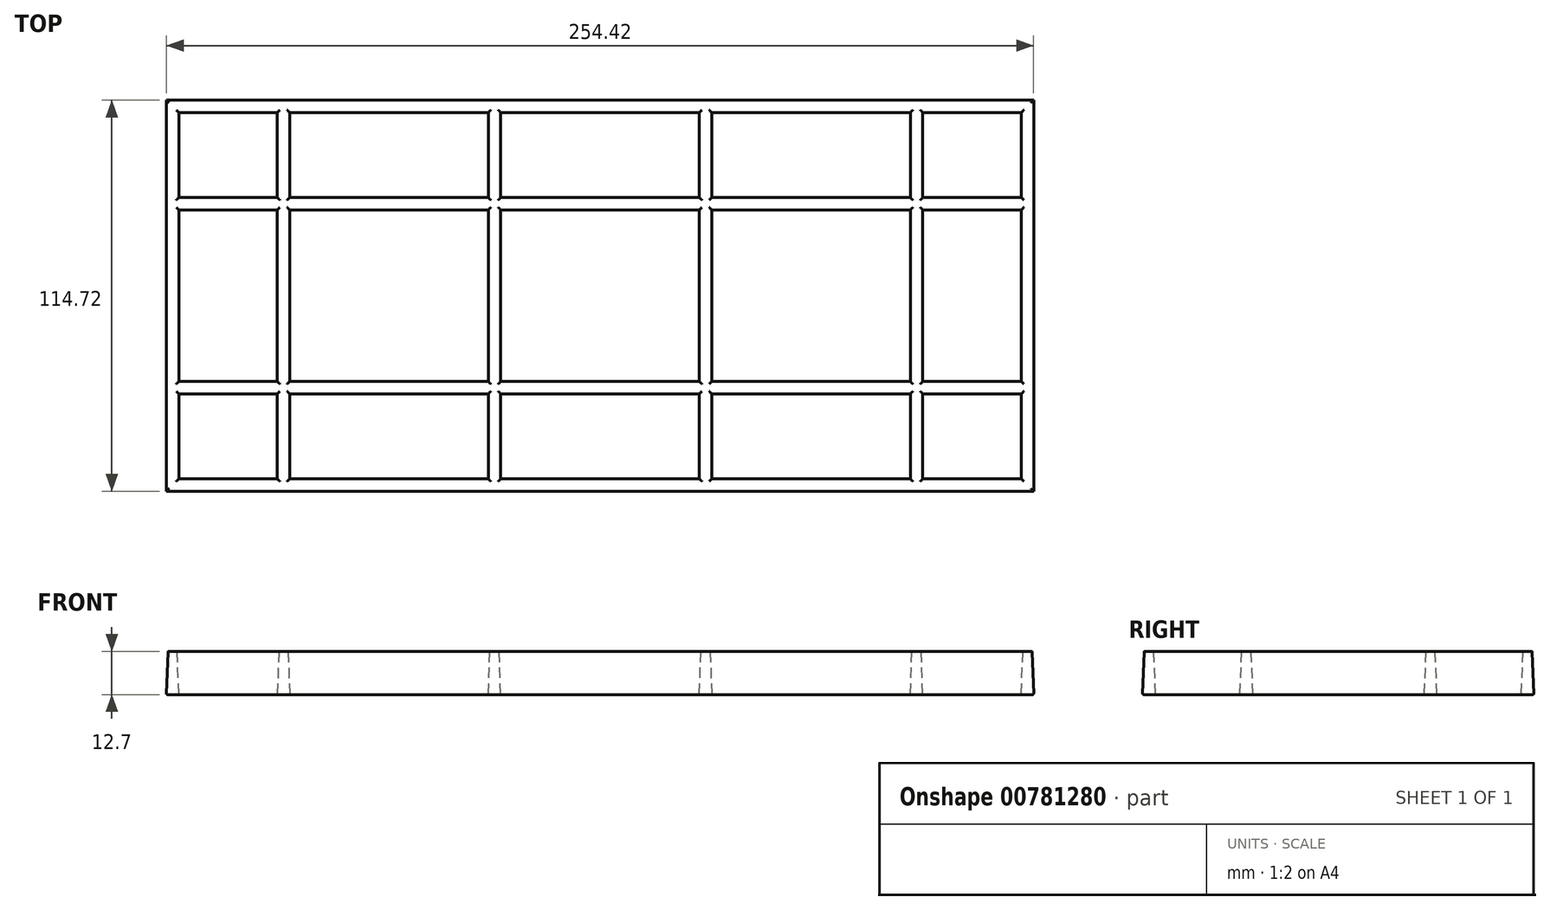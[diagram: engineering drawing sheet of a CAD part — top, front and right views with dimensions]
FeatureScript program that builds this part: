
annotation { "Feature Type Name" : "Feature", "Feature Type Description" : "" }
export const myFeature = defineFeature(function(context is Context, id is Id, definition is map)
    precondition{}
    {
        {
            var Q0;
            Q0=qCreatedBy(makeId("Top.planeOp"),FACE);
            var sketch = newSketch(context, id + "F0", { "sketchPlane" : qUnion([Q0])});
            skLineSegment(sketch, "E0.bottom", {"start": v(127, 57.15) * mm, "end": v(-127, 57.15) * mm});
            skLineSegment(sketch, "E0.top", {"start": v(127, -57.15) * mm, "end": v(-127, -57.15) * mm});
            skLineSegment(sketch, "E0.left", {"start": v(127, 57.15) * mm, "end": v(127, -57.15) * mm});
            skLineSegment(sketch, "E0.right", {"start": v(-127, 57.15) * mm, "end": v(-127, -57.15) * mm});
            skPoint(sketch, "E0.middle", {"position": v(0, 0) * mm});
            skLineSegment(sketch, "E1.0", {"start": v(123.82, 53.97) * mm, "end": v(-123.83, 53.98) * mm});
            skLineSegment(sketch, "E1.1", {"start": v(123.82, 53.97) * mm, "end": v(123.82, -53.97) * mm});
            skLineSegment(sketch, "E1.2", {"start": v(123.82, -53.98) * mm, "end": v(-123.83, -53.98) * mm});
            skLineSegment(sketch, "E1.3", {"start": v(-123.82, 53.98) * mm, "end": v(-123.83, -53.98) * mm});
            skLineSegment(sketch, "E2", {"start": v(-123.82, 26.99) * mm, "end": v(123.82, 26.99) * mm, "construction": true});
            skLineSegment(sketch, "E3", {"start": v(-123.83, 0) * mm, "end": v(123.82, 0) * mm, "construction": true});
            skLineSegment(sketch, "E4", {"start": v(-123.83, -26.99) * mm, "end": v(123.82, -26.99) * mm, "construction": true});
            skLineSegment(sketch, "E5", {"start": v(-92.87, 53.98) * mm, "end": v(-92.87, -53.98) * mm, "construction": true});
            skLineSegment(sketch, "E6", {"start": v(-61.91, 53.98) * mm, "end": v(-61.91, -53.98) * mm, "construction": true});
            skLineSegment(sketch, "E7", {"start": v(-30.96, 53.98) * mm, "end": v(-30.96, -53.98) * mm, "construction": true});
            skLineSegment(sketch, "E8", {"start": v(0, 53.98) * mm, "end": v(0, -53.98) * mm, "construction": true});
            skLineSegment(sketch, "E9", {"start": v(30.96, 53.98) * mm, "end": v(30.96, -53.98) * mm, "construction": true});
            skLineSegment(sketch, "E10", {"start": v(61.91, -53.98) * mm, "end": v(61.91, 53.98) * mm, "construction": true});
            skLineSegment(sketch, "E11", {"start": v(92.87, 53.97) * mm, "end": v(92.87, -53.97) * mm, "construction": true});
            skLineSegment(sketch, "E12.bottom", {"start": v(123.82, 28.58) * mm, "end": v(-123.82, 28.58) * mm});
            skLineSegment(sketch, "E12.top", {"start": v(123.82, 25.4) * mm, "end": v(-123.82, 25.4) * mm});
            skLineSegment(sketch, "E12.left", {"start": v(123.82, 28.58) * mm, "end": v(123.82, 25.4) * mm});
            skLineSegment(sketch, "E12.right", {"start": v(-123.82, 28.58) * mm, "end": v(-123.82, 25.4) * mm});
            skPoint(sketch, "E12.middle", {"position": v(0, 26.99) * mm});
            skLineSegment(sketch, "E13.bottom", {"start": v(123.82, 1.59) * mm, "end": v(-123.82, 1.59) * mm});
            skLineSegment(sketch, "E13.top", {"start": v(123.82, -1.59) * mm, "end": v(-123.82, -1.59) * mm});
            skLineSegment(sketch, "E13.left", {"start": v(123.82, 1.59) * mm, "end": v(123.82, -1.59) * mm});
            skLineSegment(sketch, "E13.right", {"start": v(-123.82, 1.59) * mm, "end": v(-123.82, -1.59) * mm});
            skLineSegment(sketch, "E14.bottom", {"start": v(123.82, -25.4) * mm, "end": v(-123.82, -25.4) * mm});
            skLineSegment(sketch, "E14.top", {"start": v(123.82, -28.57) * mm, "end": v(-123.82, -28.57) * mm});
            skLineSegment(sketch, "E14.left", {"start": v(123.82, -25.4) * mm, "end": v(123.82, -28.57) * mm});
            skLineSegment(sketch, "E14.right", {"start": v(-123.83, -25.4) * mm, "end": v(-123.83, -28.57) * mm});
            skPoint(sketch, "E14.middle", {"position": v(0, -26.99) * mm});
            skLineSegment(sketch, "E15.bottom", {"start": v(-91.28, 53.98) * mm, "end": v(-94.46, 53.98) * mm});
            skLineSegment(sketch, "E15.top", {"start": v(-91.28, -53.98) * mm, "end": v(-94.46, -53.98) * mm});
            skLineSegment(sketch, "E15.left", {"start": v(-91.28, 53.98) * mm, "end": v(-91.28, -53.98) * mm});
            skLineSegment(sketch, "E15.right", {"start": v(-94.46, 53.98) * mm, "end": v(-94.46, -53.98) * mm});
            skPoint(sketch, "E15.middle", {"position": v(-92.87, 0) * mm});
            skLineSegment(sketch, "E16.bottom", {"start": v(-60.32, 53.98) * mm, "end": v(-63.5, 53.98) * mm});
            skLineSegment(sketch, "E16.top", {"start": v(-60.32, -53.98) * mm, "end": v(-63.5, -53.98) * mm});
            skLineSegment(sketch, "E16.left", {"start": v(-60.32, 53.98) * mm, "end": v(-60.32, -53.98) * mm});
            skLineSegment(sketch, "E16.right", {"start": v(-63.5, 53.98) * mm, "end": v(-63.5, -53.98) * mm});
            skPoint(sketch, "E16.middle", {"position": v(-61.91, 0) * mm});
            skLineSegment(sketch, "E17.bottom", {"start": v(-29.37, 53.98) * mm, "end": v(-32.54, 53.98) * mm});
            skLineSegment(sketch, "E17.top", {"start": v(-29.37, -53.98) * mm, "end": v(-32.54, -53.98) * mm});
            skLineSegment(sketch, "E17.left", {"start": v(-29.37, 53.98) * mm, "end": v(-29.37, -53.98) * mm});
            skLineSegment(sketch, "E17.right", {"start": v(-32.54, 53.98) * mm, "end": v(-32.54, -53.98) * mm});
            skPoint(sketch, "E17.middle", {"position": v(-30.96, 0) * mm});
            skLineSegment(sketch, "E18.bottom", {"start": v(1.59, 53.98) * mm, "end": v(-1.59, 53.98) * mm});
            skLineSegment(sketch, "E18.top", {"start": v(1.59, -53.98) * mm, "end": v(-1.59, -53.98) * mm});
            skLineSegment(sketch, "E18.left", {"start": v(1.59, 53.98) * mm, "end": v(1.59, -53.98) * mm});
            skLineSegment(sketch, "E18.right", {"start": v(-1.59, 53.98) * mm, "end": v(-1.59, -53.98) * mm});
            skLineSegment(sketch, "E19.bottom", {"start": v(32.54, 53.98) * mm, "end": v(29.37, 53.98) * mm});
            skLineSegment(sketch, "E19.top", {"start": v(32.54, -53.98) * mm, "end": v(29.37, -53.98) * mm});
            skLineSegment(sketch, "E19.left", {"start": v(32.54, 53.98) * mm, "end": v(32.54, -53.98) * mm});
            skLineSegment(sketch, "E19.right", {"start": v(29.37, 53.98) * mm, "end": v(29.37, -53.98) * mm});
            skPoint(sketch, "E19.middle", {"position": v(30.96, 0) * mm});
            skLineSegment(sketch, "E20.bottom", {"start": v(63.5, 53.98) * mm, "end": v(60.33, 53.98) * mm});
            skLineSegment(sketch, "E20.top", {"start": v(63.5, -53.98) * mm, "end": v(60.33, -53.98) * mm});
            skLineSegment(sketch, "E20.left", {"start": v(63.5, 53.98) * mm, "end": v(63.5, -53.98) * mm});
            skLineSegment(sketch, "E20.right", {"start": v(60.33, 53.98) * mm, "end": v(60.33, -53.98) * mm});
            skPoint(sketch, "E20.middle", {"position": v(61.91, 0) * mm});
            skLineSegment(sketch, "E21.bottom", {"start": v(94.46, 53.97) * mm, "end": v(91.28, 53.97) * mm});
            skLineSegment(sketch, "E21.top", {"start": v(94.46, -53.97) * mm, "end": v(91.28, -53.97) * mm});
            skLineSegment(sketch, "E21.left", {"start": v(94.46, 53.98) * mm, "end": v(94.46, -53.98) * mm});
            skLineSegment(sketch, "E21.right", {"start": v(91.28, 53.98) * mm, "end": v(91.28, -53.98) * mm});
            skPoint(sketch, "E21.middle", {"position": v(92.87, 0) * mm});
            skSolve(sketch);
        }
        {
            var Q0;
            Q0=makeQuery(id+"F0.imprint","IMPRINT",FACE,{"disambiguationData":[TD([[makeQuery(id+"F0.imprint","IMPRINT",EDGE,{"derivedFrom":sQuery(id+"F0.wireOp",EDGE,"E0.bottom")}),1.0]])]});
            var Q1;
            {var subQ0=sQuery(id+"F0.wireOp",EDGE,"E20.left");var subQ1=sQuery(id+"F0.wireOp",EDGE,"E12.bottom");var subQ2=makeQuery(id+"F0.imprint","INTERSECT",VERTEX,{"derivedFrom":[subQ1,subQ0]});Q1=makeQuery(id+"F0.imprint","IMPRINT",FACE,{"disambiguationData":[TD([[makeQuery(id+"F0.imprint","IMPRINT",EDGE,{"disambiguationData":[TD([[subQ2,-1.0]])],"derivedFrom":subQ1}),1.0]])]});}
            var Q2;
            {var subQ0=sQuery(id+"F0.wireOp",EDGE,"E18.left");var subQ1=sQuery(id+"F0.wireOp",EDGE,"E12.bottom");var subQ2=makeQuery(id+"F0.imprint","INTERSECT",VERTEX,{"derivedFrom":[subQ1,subQ0]});Q2=makeQuery(id+"F0.imprint","IMPRINT",FACE,{"disambiguationData":[TD([[makeQuery(id+"F0.imprint","IMPRINT",EDGE,{"disambiguationData":[TD([[subQ2,-1.0]])],"derivedFrom":subQ1}),1.0]])]});}
            var Q3;
            {var subQ0=sQuery(id+"F0.wireOp",EDGE,"E16.right");var subQ1=sQuery(id+"F0.wireOp",EDGE,"E12.bottom");var subQ2=makeQuery(id+"F0.imprint","INTERSECT",VERTEX,{"derivedFrom":[subQ1,subQ0]});Q3=makeQuery(id+"F0.imprint","IMPRINT",FACE,{"disambiguationData":[TD([[makeQuery(id+"F0.imprint","IMPRINT",EDGE,{"disambiguationData":[TD([[subQ2,1.0]])],"derivedFrom":subQ1}),1.0]])]});}
            var Q4;
            {var subQ0=sQuery(id+"F0.wireOp",EDGE,"E21.left");var subQ1=sQuery(id+"F0.wireOp",EDGE,"E13.bottom");var subQ2=makeQuery(id+"F0.imprint","INTERSECT",VERTEX,{"derivedFrom":[subQ1,subQ0]});Q4=makeQuery(id+"F0.imprint","IMPRINT",FACE,{"disambiguationData":[TD([[makeQuery(id+"F0.imprint","IMPRINT",EDGE,{"disambiguationData":[TD([[subQ2,-1.0]])],"derivedFrom":subQ1}),1.0]])]});}
            var Q5;
            {var subQ0=sQuery(id+"F0.wireOp",EDGE,"E19.right");var subQ1=sQuery(id+"F0.wireOp",EDGE,"E13.bottom");var subQ2=makeQuery(id+"F0.imprint","INTERSECT",VERTEX,{"derivedFrom":[subQ1,subQ0]});Q5=makeQuery(id+"F0.imprint","IMPRINT",FACE,{"disambiguationData":[TD([[makeQuery(id+"F0.imprint","IMPRINT",EDGE,{"disambiguationData":[TD([[subQ2,1.0]])],"derivedFrom":subQ1}),1.0]])]});}
            var Q6;
            {var subQ0=sQuery(id+"F0.wireOp",EDGE,"E15.right");var subQ1=sQuery(id+"F0.wireOp",EDGE,"E13.bottom");var subQ2=makeQuery(id+"F0.imprint","INTERSECT",VERTEX,{"derivedFrom":[subQ1,subQ0]});Q6=makeQuery(id+"F0.imprint","IMPRINT",FACE,{"disambiguationData":[TD([[makeQuery(id+"F0.imprint","IMPRINT",EDGE,{"disambiguationData":[TD([[subQ2,1.0]])],"derivedFrom":subQ1}),1.0]])]});}
            var Q7;
            {var subQ0=sQuery(id+"F0.wireOp",EDGE,"E17.right");var subQ1=sQuery(id+"F0.wireOp",EDGE,"E13.bottom");var subQ2=makeQuery(id+"F0.imprint","INTERSECT",VERTEX,{"derivedFrom":[subQ1,subQ0]});Q7=makeQuery(id+"F0.imprint","IMPRINT",FACE,{"disambiguationData":[TD([[makeQuery(id+"F0.imprint","IMPRINT",EDGE,{"disambiguationData":[TD([[subQ2,1.0]])],"derivedFrom":subQ1}),1.0]])]});}
            var Q8;
            {var subQ0=sQuery(id+"F0.wireOp",EDGE,"E20.left");var subQ1=sQuery(id+"F0.wireOp",EDGE,"E14.bottom");var subQ2=makeQuery(id+"F0.imprint","INTERSECT",VERTEX,{"derivedFrom":[subQ1,subQ0]});Q8=makeQuery(id+"F0.imprint","IMPRINT",FACE,{"disambiguationData":[TD([[makeQuery(id+"F0.imprint","IMPRINT",EDGE,{"disambiguationData":[TD([[subQ2,-1.0]])],"derivedFrom":subQ1}),1.0]])]});}
            var Q9;
            {var subQ0=sQuery(id+"F0.wireOp",EDGE,"E18.left");var subQ1=sQuery(id+"F0.wireOp",EDGE,"E14.bottom");var subQ2=makeQuery(id+"F0.imprint","INTERSECT",VERTEX,{"derivedFrom":[subQ1,subQ0]});Q9=makeQuery(id+"F0.imprint","IMPRINT",FACE,{"disambiguationData":[TD([[makeQuery(id+"F0.imprint","IMPRINT",EDGE,{"disambiguationData":[TD([[subQ2,-1.0]])],"derivedFrom":subQ1}),1.0]])]});}
            var Q10;
            {var subQ0=sQuery(id+"F0.wireOp",EDGE,"E16.left");var subQ1=sQuery(id+"F0.wireOp",EDGE,"E14.bottom");var subQ2=makeQuery(id+"F0.imprint","INTERSECT",VERTEX,{"derivedFrom":[subQ1,subQ0]});Q10=makeQuery(id+"F0.imprint","IMPRINT",FACE,{"disambiguationData":[TD([[makeQuery(id+"F0.imprint","IMPRINT",EDGE,{"disambiguationData":[TD([[subQ2,-1.0]])],"derivedFrom":subQ1}),1.0]])]});}
            var Q11;
            {var subQ0=sQuery(id+"F0.wireOp",EDGE,"E15.right");var subQ1=sQuery(id+"F0.wireOp",EDGE,"E12.bottom");var subQ2=makeQuery(id+"F0.imprint","INTERSECT",VERTEX,{"derivedFrom":[subQ1,subQ0]});Q11=makeQuery(id+"F0.imprint","IMPRINT",FACE,{"disambiguationData":[TD([[makeQuery(id+"F0.imprint","IMPRINT",EDGE,{"disambiguationData":[TD([[subQ2,1.0]])],"derivedFrom":subQ1}),1.0]])]});}
            var Q12;
            {var subQ0=sQuery(id+"F0.wireOp",EDGE,"E12.top");var subQ1=sQuery(id+"F0.wireOp",EDGE,"E1.3");var subQ2=makeQuery(id+"F0.imprint","INTERSECT",VERTEX,{"derivedFrom":[subQ1,subQ0]});Q12=makeQuery(id+"F0.imprint","IMPRINT",FACE,{"disambiguationData":[TD([[makeQuery(id+"F0.imprint","IMPRINT",EDGE,{"disambiguationData":[TD([[subQ2,1.0]])],"derivedFrom":subQ1}),1.0]])]});}
            var Q13;
            {var subQ0=sQuery(id+"F0.wireOp",EDGE,"E15.right");var subQ1=sQuery(id+"F0.wireOp",EDGE,"E1.0");var subQ2=makeQuery(id+"F0.imprint","INTERSECT",VERTEX,{"derivedFrom":[subQ1,subQ0]});Q13=makeQuery(id+"F0.imprint","IMPRINT",FACE,{"disambiguationData":[TD([[makeQuery(id+"F0.imprint","IMPRINT",EDGE,{"disambiguationData":[TD([[subQ2,1.0]])],"derivedFrom":subQ1}),1.0]])]});}
            var Q14;
            {var subQ0=sQuery(id+"F0.wireOp",EDGE,"E15.right");var subQ1=sQuery(id+"F0.wireOp",EDGE,"E12.top");var subQ2=makeQuery(id+"F0.imprint","INTERSECT",VERTEX,{"derivedFrom":[subQ1,subQ0]});Q14=makeQuery(id+"F0.imprint","IMPRINT",FACE,{"disambiguationData":[TD([[makeQuery(id+"F0.imprint","IMPRINT",EDGE,{"disambiguationData":[TD([[subQ2,1.0]])],"derivedFrom":subQ1}),1.0]])]});}
            var Q15;
            {var subQ0=sQuery(id+"F0.wireOp",EDGE,"E16.right");var subQ1=sQuery(id+"F0.wireOp",EDGE,"E12.bottom");var subQ2=makeQuery(id+"F0.imprint","INTERSECT",VERTEX,{"derivedFrom":[subQ1,subQ0]});Q15=makeQuery(id+"F0.imprint","IMPRINT",FACE,{"disambiguationData":[TD([[makeQuery(id+"F0.imprint","IMPRINT",EDGE,{"disambiguationData":[TD([[subQ2,-1.0]])],"derivedFrom":subQ1}),1.0]])]});}
            var Q16;
            {var subQ0=sQuery(id+"F0.wireOp",EDGE,"E15.right");var subQ1=sQuery(id+"F0.wireOp",EDGE,"E13.top");var subQ2=makeQuery(id+"F0.imprint","INTERSECT",VERTEX,{"derivedFrom":[subQ1,subQ0]});Q16=makeQuery(id+"F0.imprint","IMPRINT",FACE,{"disambiguationData":[TD([[makeQuery(id+"F0.imprint","IMPRINT",EDGE,{"disambiguationData":[TD([[subQ2,1.0]])],"derivedFrom":subQ1}),1.0]])]});}
            var Q17;
            {var subQ0=sQuery(id+"F0.wireOp",EDGE,"E15.right");var subQ1=sQuery(id+"F0.wireOp",EDGE,"E14.bottom");var subQ2=makeQuery(id+"F0.imprint","INTERSECT",VERTEX,{"derivedFrom":[subQ1,subQ0]});Q17=makeQuery(id+"F0.imprint","IMPRINT",FACE,{"disambiguationData":[TD([[makeQuery(id+"F0.imprint","IMPRINT",EDGE,{"disambiguationData":[TD([[subQ2,1.0]])],"derivedFrom":subQ1}),1.0]])]});}
            var Q18;
            {var subQ0=sQuery(id+"F0.wireOp",EDGE,"E15.right");var subQ1=sQuery(id+"F0.wireOp",EDGE,"E1.2");var subQ2=makeQuery(id+"F0.imprint","INTERSECT",VERTEX,{"derivedFrom":[subQ1,subQ0]});Q18=makeQuery(id+"F0.imprint","IMPRINT",FACE,{"disambiguationData":[TD([[makeQuery(id+"F0.imprint","IMPRINT",EDGE,{"disambiguationData":[TD([[subQ2,1.0]])],"derivedFrom":subQ1}),-1.0]])]});}
            var Q19;
            {var subQ0=sQuery(id+"F0.wireOp",EDGE,"E14.top");var subQ1=sQuery(id+"F0.wireOp",EDGE,"E1.3");var subQ2=makeQuery(id+"F0.imprint","INTERSECT",VERTEX,{"derivedFrom":[subQ1,subQ0]});Q19=makeQuery(id+"F0.imprint","IMPRINT",FACE,{"disambiguationData":[TD([[makeQuery(id+"F0.imprint","IMPRINT",EDGE,{"disambiguationData":[TD([[subQ2,1.0]])],"derivedFrom":subQ1}),1.0]])]});}
            var Q20;
            {var subQ0=sQuery(id+"F0.wireOp",EDGE,"E16.right");var subQ1=sQuery(id+"F0.wireOp",EDGE,"E14.bottom");var subQ2=makeQuery(id+"F0.imprint","INTERSECT",VERTEX,{"derivedFrom":[subQ1,subQ0]});Q20=makeQuery(id+"F0.imprint","IMPRINT",FACE,{"disambiguationData":[TD([[makeQuery(id+"F0.imprint","IMPRINT",EDGE,{"disambiguationData":[TD([[subQ2,-1.0]])],"derivedFrom":subQ1}),1.0]])]});}
            var Q21;
            {var subQ0=sQuery(id+"F0.wireOp",EDGE,"E17.right");var subQ1=sQuery(id+"F0.wireOp",EDGE,"E12.bottom");var subQ2=makeQuery(id+"F0.imprint","INTERSECT",VERTEX,{"derivedFrom":[subQ1,subQ0]});Q21=makeQuery(id+"F0.imprint","IMPRINT",FACE,{"disambiguationData":[TD([[makeQuery(id+"F0.imprint","IMPRINT",EDGE,{"disambiguationData":[TD([[subQ2,-1.0]])],"derivedFrom":subQ1}),1.0]])]});}
            var Q22;
            {var subQ0=sQuery(id+"F0.wireOp",EDGE,"E17.right");var subQ1=sQuery(id+"F0.wireOp",EDGE,"E1.0");var subQ2=makeQuery(id+"F0.imprint","INTERSECT",VERTEX,{"derivedFrom":[subQ1,subQ0]});Q22=makeQuery(id+"F0.imprint","IMPRINT",FACE,{"disambiguationData":[TD([[makeQuery(id+"F0.imprint","IMPRINT",EDGE,{"disambiguationData":[TD([[subQ2,1.0]])],"derivedFrom":subQ1}),1.0]])]});}
            var Q23;
            {var subQ0=sQuery(id+"F0.wireOp",EDGE,"E17.right");var subQ1=sQuery(id+"F0.wireOp",EDGE,"E12.top");var subQ2=makeQuery(id+"F0.imprint","INTERSECT",VERTEX,{"derivedFrom":[subQ1,subQ0]});Q23=makeQuery(id+"F0.imprint","IMPRINT",FACE,{"disambiguationData":[TD([[makeQuery(id+"F0.imprint","IMPRINT",EDGE,{"disambiguationData":[TD([[subQ2,1.0]])],"derivedFrom":subQ1}),1.0]])]});}
            var Q24;
            {var subQ0=sQuery(id+"F0.wireOp",EDGE,"E17.left");var subQ1=sQuery(id+"F0.wireOp",EDGE,"E12.bottom");var subQ2=makeQuery(id+"F0.imprint","INTERSECT",VERTEX,{"derivedFrom":[subQ1,subQ0]});Q24=makeQuery(id+"F0.imprint","IMPRINT",FACE,{"disambiguationData":[TD([[makeQuery(id+"F0.imprint","IMPRINT",EDGE,{"disambiguationData":[TD([[subQ2,1.0]])],"derivedFrom":subQ1}),1.0]])]});}
            var Q25;
            {var subQ0=sQuery(id+"F0.wireOp",EDGE,"E17.right");var subQ1=sQuery(id+"F0.wireOp",EDGE,"E13.top");var subQ2=makeQuery(id+"F0.imprint","INTERSECT",VERTEX,{"derivedFrom":[subQ1,subQ0]});Q25=makeQuery(id+"F0.imprint","IMPRINT",FACE,{"disambiguationData":[TD([[makeQuery(id+"F0.imprint","IMPRINT",EDGE,{"disambiguationData":[TD([[subQ2,1.0]])],"derivedFrom":subQ1}),1.0]])]});}
            var Q26;
            {var subQ0=sQuery(id+"F0.wireOp",EDGE,"E17.right");var subQ1=sQuery(id+"F0.wireOp",EDGE,"E14.bottom");var subQ2=makeQuery(id+"F0.imprint","INTERSECT",VERTEX,{"derivedFrom":[subQ1,subQ0]});Q26=makeQuery(id+"F0.imprint","IMPRINT",FACE,{"disambiguationData":[TD([[makeQuery(id+"F0.imprint","IMPRINT",EDGE,{"disambiguationData":[TD([[subQ2,1.0]])],"derivedFrom":subQ1}),1.0]])]});}
            var Q27;
            {var subQ0=sQuery(id+"F0.wireOp",EDGE,"E17.right");var subQ1=sQuery(id+"F0.wireOp",EDGE,"E14.bottom");var subQ2=makeQuery(id+"F0.imprint","INTERSECT",VERTEX,{"derivedFrom":[subQ1,subQ0]});Q27=makeQuery(id+"F0.imprint","IMPRINT",FACE,{"disambiguationData":[TD([[makeQuery(id+"F0.imprint","IMPRINT",EDGE,{"disambiguationData":[TD([[subQ2,-1.0]])],"derivedFrom":subQ1}),1.0]])]});}
            var Q28;
            {var subQ0=sQuery(id+"F0.wireOp",EDGE,"E17.right");var subQ1=sQuery(id+"F0.wireOp",EDGE,"E1.2");var subQ2=makeQuery(id+"F0.imprint","INTERSECT",VERTEX,{"derivedFrom":[subQ1,subQ0]});Q28=makeQuery(id+"F0.imprint","IMPRINT",FACE,{"disambiguationData":[TD([[makeQuery(id+"F0.imprint","IMPRINT",EDGE,{"disambiguationData":[TD([[subQ2,1.0]])],"derivedFrom":subQ1}),-1.0]])]});}
            var Q29;
            {var subQ0=sQuery(id+"F0.wireOp",EDGE,"E17.left");var subQ1=sQuery(id+"F0.wireOp",EDGE,"E14.bottom");var subQ2=makeQuery(id+"F0.imprint","INTERSECT",VERTEX,{"derivedFrom":[subQ1,subQ0]});Q29=makeQuery(id+"F0.imprint","IMPRINT",FACE,{"disambiguationData":[TD([[makeQuery(id+"F0.imprint","IMPRINT",EDGE,{"disambiguationData":[TD([[subQ2,1.0]])],"derivedFrom":subQ1}),1.0]])]});}
            var Q30;
            {var subQ0=sQuery(id+"F0.wireOp",EDGE,"E17.right");var subQ1=sQuery(id+"F0.wireOp",EDGE,"E12.bottom");var subQ2=makeQuery(id+"F0.imprint","INTERSECT",VERTEX,{"derivedFrom":[subQ1,subQ0]});Q30=makeQuery(id+"F0.imprint","IMPRINT",FACE,{"disambiguationData":[TD([[makeQuery(id+"F0.imprint","IMPRINT",EDGE,{"disambiguationData":[TD([[subQ2,1.0]])],"derivedFrom":subQ1}),1.0]])]});}
            var Q31;
            {var subQ0=sQuery(id+"F0.wireOp",EDGE,"E19.right");var subQ1=sQuery(id+"F0.wireOp",EDGE,"E1.2");var subQ2=makeQuery(id+"F0.imprint","INTERSECT",VERTEX,{"derivedFrom":[subQ1,subQ0]});Q31=makeQuery(id+"F0.imprint","IMPRINT",FACE,{"disambiguationData":[TD([[makeQuery(id+"F0.imprint","IMPRINT",EDGE,{"disambiguationData":[TD([[subQ2,1.0]])],"derivedFrom":subQ1}),-1.0]])]});}
            var Q32;
            {var subQ0=sQuery(id+"F0.wireOp",EDGE,"E19.right");var subQ1=sQuery(id+"F0.wireOp",EDGE,"E14.bottom");var subQ2=makeQuery(id+"F0.imprint","INTERSECT",VERTEX,{"derivedFrom":[subQ1,subQ0]});Q32=makeQuery(id+"F0.imprint","IMPRINT",FACE,{"disambiguationData":[TD([[makeQuery(id+"F0.imprint","IMPRINT",EDGE,{"disambiguationData":[TD([[subQ2,1.0]])],"derivedFrom":subQ1}),1.0]])]});}
            var Q33;
            {var subQ0=sQuery(id+"F0.wireOp",EDGE,"E19.right");var subQ1=sQuery(id+"F0.wireOp",EDGE,"E13.top");var subQ2=makeQuery(id+"F0.imprint","INTERSECT",VERTEX,{"derivedFrom":[subQ1,subQ0]});Q33=makeQuery(id+"F0.imprint","IMPRINT",FACE,{"disambiguationData":[TD([[makeQuery(id+"F0.imprint","IMPRINT",EDGE,{"disambiguationData":[TD([[subQ2,1.0]])],"derivedFrom":subQ1}),1.0]])]});}
            var Q34;
            {var subQ0=sQuery(id+"F0.wireOp",EDGE,"E19.right");var subQ1=sQuery(id+"F0.wireOp",EDGE,"E14.bottom");var subQ2=makeQuery(id+"F0.imprint","INTERSECT",VERTEX,{"derivedFrom":[subQ1,subQ0]});Q34=makeQuery(id+"F0.imprint","IMPRINT",FACE,{"disambiguationData":[TD([[makeQuery(id+"F0.imprint","IMPRINT",EDGE,{"disambiguationData":[TD([[subQ2,-1.0]])],"derivedFrom":subQ1}),1.0]])]});}
            var Q35;
            {var subQ0=sQuery(id+"F0.wireOp",EDGE,"E20.right");var subQ1=sQuery(id+"F0.wireOp",EDGE,"E14.bottom");var subQ2=makeQuery(id+"F0.imprint","INTERSECT",VERTEX,{"derivedFrom":[subQ1,subQ0]});Q35=makeQuery(id+"F0.imprint","IMPRINT",FACE,{"disambiguationData":[TD([[makeQuery(id+"F0.imprint","IMPRINT",EDGE,{"disambiguationData":[TD([[subQ2,-1.0]])],"derivedFrom":subQ1}),1.0]])]});}
            var Q36;
            {var subQ0=sQuery(id+"F0.wireOp",EDGE,"E19.right");var subQ1=sQuery(id+"F0.wireOp",EDGE,"E12.top");var subQ2=makeQuery(id+"F0.imprint","INTERSECT",VERTEX,{"derivedFrom":[subQ1,subQ0]});Q36=makeQuery(id+"F0.imprint","IMPRINT",FACE,{"disambiguationData":[TD([[makeQuery(id+"F0.imprint","IMPRINT",EDGE,{"disambiguationData":[TD([[subQ2,1.0]])],"derivedFrom":subQ1}),1.0]])]});}
            var Q37;
            {var subQ0=sQuery(id+"F0.wireOp",EDGE,"E19.right");var subQ1=sQuery(id+"F0.wireOp",EDGE,"E1.0");var subQ2=makeQuery(id+"F0.imprint","INTERSECT",VERTEX,{"derivedFrom":[subQ1,subQ0]});Q37=makeQuery(id+"F0.imprint","IMPRINT",FACE,{"disambiguationData":[TD([[makeQuery(id+"F0.imprint","IMPRINT",EDGE,{"disambiguationData":[TD([[subQ2,1.0]])],"derivedFrom":subQ1}),1.0]])]});}
            var Q38;
            {var subQ0=sQuery(id+"F0.wireOp",EDGE,"E19.right");var subQ1=sQuery(id+"F0.wireOp",EDGE,"E12.bottom");var subQ2=makeQuery(id+"F0.imprint","INTERSECT",VERTEX,{"derivedFrom":[subQ1,subQ0]});Q38=makeQuery(id+"F0.imprint","IMPRINT",FACE,{"disambiguationData":[TD([[makeQuery(id+"F0.imprint","IMPRINT",EDGE,{"disambiguationData":[TD([[subQ2,1.0]])],"derivedFrom":subQ1}),1.0]])]});}
            var Q39;
            {var subQ0=sQuery(id+"F0.wireOp",EDGE,"E19.right");var subQ1=sQuery(id+"F0.wireOp",EDGE,"E12.bottom");var subQ2=makeQuery(id+"F0.imprint","INTERSECT",VERTEX,{"derivedFrom":[subQ1,subQ0]});Q39=makeQuery(id+"F0.imprint","IMPRINT",FACE,{"disambiguationData":[TD([[makeQuery(id+"F0.imprint","IMPRINT",EDGE,{"disambiguationData":[TD([[subQ2,-1.0]])],"derivedFrom":subQ1}),1.0]])]});}
            var Q40;
            {var subQ0=sQuery(id+"F0.wireOp",EDGE,"E19.left");var subQ1=sQuery(id+"F0.wireOp",EDGE,"E12.bottom");var subQ2=makeQuery(id+"F0.imprint","INTERSECT",VERTEX,{"derivedFrom":[subQ1,subQ0]});Q40=makeQuery(id+"F0.imprint","IMPRINT",FACE,{"disambiguationData":[TD([[makeQuery(id+"F0.imprint","IMPRINT",EDGE,{"disambiguationData":[TD([[subQ2,1.0]])],"derivedFrom":subQ1}),1.0]])]});}
            var Q41;
            {var subQ0=sQuery(id+"F0.wireOp",EDGE,"E21.right");var subQ1=sQuery(id+"F0.wireOp",EDGE,"E12.top");var subQ2=makeQuery(id+"F0.imprint","INTERSECT",VERTEX,{"derivedFrom":[subQ1,subQ0]});Q41=makeQuery(id+"F0.imprint","IMPRINT",FACE,{"disambiguationData":[TD([[makeQuery(id+"F0.imprint","IMPRINT",EDGE,{"disambiguationData":[TD([[subQ2,1.0]])],"derivedFrom":subQ1}),1.0]])]});}
            var Q42;
            {var subQ0=sQuery(id+"F0.wireOp",EDGE,"E21.left");var subQ1=sQuery(id+"F0.wireOp",EDGE,"E12.bottom");var subQ2=makeQuery(id+"F0.imprint","INTERSECT",VERTEX,{"derivedFrom":[subQ1,subQ0]});Q42=makeQuery(id+"F0.imprint","IMPRINT",FACE,{"disambiguationData":[TD([[makeQuery(id+"F0.imprint","IMPRINT",EDGE,{"disambiguationData":[TD([[subQ2,-1.0]])],"derivedFrom":subQ1}),1.0]])]});}
            var Q43;
            {var subQ0=sQuery(id+"F0.wireOp",EDGE,"E21.left");var subQ1=sQuery(id+"F0.wireOp",EDGE,"E1.0");var subQ2=makeQuery(id+"F0.imprint","INTERSECT",VERTEX,{"derivedFrom":[subQ1,subQ0]});Q43=makeQuery(id+"F0.imprint","IMPRINT",FACE,{"disambiguationData":[TD([[makeQuery(id+"F0.imprint","IMPRINT",EDGE,{"disambiguationData":[TD([[subQ2,-1.0]])],"derivedFrom":subQ1}),1.0]])]});}
            var Q44;
            {var subQ0=sQuery(id+"F0.wireOp",EDGE,"E21.right");var subQ1=sQuery(id+"F0.wireOp",EDGE,"E12.bottom");var subQ2=makeQuery(id+"F0.imprint","INTERSECT",VERTEX,{"derivedFrom":[subQ1,subQ0]});Q44=makeQuery(id+"F0.imprint","IMPRINT",FACE,{"disambiguationData":[TD([[makeQuery(id+"F0.imprint","IMPRINT",EDGE,{"disambiguationData":[TD([[subQ2,-1.0]])],"derivedFrom":subQ1}),1.0]])]});}
            var Q45;
            {var subQ0=sQuery(id+"F0.wireOp",EDGE,"E12.top");var subQ1=sQuery(id+"F0.wireOp",EDGE,"E1.1");var subQ2=makeQuery(id+"F0.imprint","INTERSECT",VERTEX,{"derivedFrom":[subQ1,subQ0]});Q45=makeQuery(id+"F0.imprint","IMPRINT",FACE,{"disambiguationData":[TD([[makeQuery(id+"F0.imprint","IMPRINT",EDGE,{"disambiguationData":[TD([[subQ2,1.0]])],"derivedFrom":subQ1}),-1.0]])]});}
            var Q46;
            {var subQ0=sQuery(id+"F0.wireOp",EDGE,"E21.right");var subQ1=sQuery(id+"F0.wireOp",EDGE,"E14.bottom");var subQ2=makeQuery(id+"F0.imprint","INTERSECT",VERTEX,{"derivedFrom":[subQ1,subQ0]});Q46=makeQuery(id+"F0.imprint","IMPRINT",FACE,{"disambiguationData":[TD([[makeQuery(id+"F0.imprint","IMPRINT",EDGE,{"disambiguationData":[TD([[subQ2,-1.0]])],"derivedFrom":subQ1}),1.0]])]});}
            var Q47;
            {var subQ0=sQuery(id+"F0.wireOp",EDGE,"E21.left");var subQ1=sQuery(id+"F0.wireOp",EDGE,"E13.top");var subQ2=makeQuery(id+"F0.imprint","INTERSECT",VERTEX,{"derivedFrom":[subQ1,subQ0]});Q47=makeQuery(id+"F0.imprint","IMPRINT",FACE,{"disambiguationData":[TD([[makeQuery(id+"F0.imprint","IMPRINT",EDGE,{"disambiguationData":[TD([[subQ2,-1.0]])],"derivedFrom":subQ1}),1.0]])]});}
            var Q48;
            {var subQ0=sQuery(id+"F0.wireOp",EDGE,"E21.left");var subQ1=sQuery(id+"F0.wireOp",EDGE,"E14.bottom");var subQ2=makeQuery(id+"F0.imprint","INTERSECT",VERTEX,{"derivedFrom":[subQ1,subQ0]});Q48=makeQuery(id+"F0.imprint","IMPRINT",FACE,{"disambiguationData":[TD([[makeQuery(id+"F0.imprint","IMPRINT",EDGE,{"disambiguationData":[TD([[subQ2,-1.0]])],"derivedFrom":subQ1}),1.0]])]});}
            var Q49;
            {var subQ0=sQuery(id+"F0.wireOp",EDGE,"E21.left");var subQ1=sQuery(id+"F0.wireOp",EDGE,"E1.2");var subQ2=makeQuery(id+"F0.imprint","INTERSECT",VERTEX,{"derivedFrom":[subQ1,subQ0]});Q49=makeQuery(id+"F0.imprint","IMPRINT",FACE,{"disambiguationData":[TD([[makeQuery(id+"F0.imprint","IMPRINT",EDGE,{"disambiguationData":[TD([[subQ2,-1.0]])],"derivedFrom":subQ1}),-1.0]])]});}
            var Q50;
            {var subQ0=sQuery(id+"F0.wireOp",EDGE,"E14.top");var subQ1=sQuery(id+"F0.wireOp",EDGE,"E1.1");var subQ2=makeQuery(id+"F0.imprint","INTERSECT",VERTEX,{"derivedFrom":[subQ1,subQ0]});Q50=makeQuery(id+"F0.imprint","IMPRINT",FACE,{"disambiguationData":[TD([[makeQuery(id+"F0.imprint","IMPRINT",EDGE,{"disambiguationData":[TD([[subQ2,1.0]])],"derivedFrom":subQ1}),-1.0]])]});}
            extrude(context, id + "F1", {"entities" : qUnion([Q0, Q1, Q2, Q3, Q4, Q5, Q6, Q7, Q8, Q9, Q10, Q11, Q12, Q13, Q14, Q15, Q16, Q17, Q18, Q19, Q20, Q21, Q22, Q23, Q24, Q25, Q26, Q27, Q28, Q29, Q30, Q31, Q32, Q33, Q34, Q35, Q36, Q37, Q38, Q39, Q40, Q41, Q42, Q43, Q44, Q45, Q46, Q47, Q48, Q49, Q50]), "depth" : 6.35 * mm, "offsetDistance" : 25.4 * mm, "hasDraft" : true, "draftAngle" : 2 * degree, "draftPullDirection" : true});
        }
        {
            var Q0;
            Q0=makeQuery(id+"F1.opExtrude","CAP_FACE",FACE,{"disambiguationData":[OSD([sQuery(id+"F0.wireOp",EDGE,"E0.bottom"),sQuery(id+"F0.wireOp",EDGE,"E0.top"),sQuery(id+"F0.wireOp",EDGE,"E0.left"),sQuery(id+"F0.wireOp",EDGE,"E0.right"),sQuery(id+"F0.wireOp",EDGE,"E1.0"),sQuery(id+"F0.wireOp",EDGE,"E1.1"),sQuery(id+"F0.wireOp",EDGE,"E1.2"),sQuery(id+"F0.wireOp",EDGE,"E1.3"),sQuery(id+"F0.wireOp",EDGE,"E12.bottom"),sQuery(id+"F0.wireOp",EDGE,"E12.top"),sQuery(id+"F0.wireOp",EDGE,"E14.bottom"),sQuery(id+"F0.wireOp",EDGE,"E14.top"),sQuery(id+"F0.wireOp",EDGE,"E15.left"),sQuery(id+"F0.wireOp",EDGE,"E15.right"),sQuery(id+"F0.wireOp",EDGE,"E17.left"),sQuery(id+"F0.wireOp",EDGE,"E17.right"),sQuery(id+"F0.wireOp",EDGE,"E19.left"),sQuery(id+"F0.wireOp",EDGE,"E19.right"),sQuery(id+"F0.wireOp",EDGE,"E21.left"),sQuery(id+"F0.wireOp",EDGE,"E21.right")])],"isStart":true});
            var sketch = newSketch(context, id + "F2", { "sketchPlane" : qUnion([Q0])});
            skLineSegment(sketch, "E22.bottom", {"start": v(-123.83, 25.4) * mm, "end": v(-94.46, 25.4) * mm});
            skLineSegment(sketch, "E22.top", {"start": v(-123.83, -25.4) * mm, "end": v(-94.46, -25.4) * mm});
            skLineSegment(sketch, "E22.left", {"start": v(-123.83, 25.4) * mm, "end": v(-123.83, -25.4) * mm});
            skLineSegment(sketch, "E22.right", {"start": v(-94.46, 25.4) * mm, "end": v(-94.46, -25.4) * mm});
            skLineSegment(sketch, "E23.bottom", {"start": v(-123.82, -28.58) * mm, "end": v(-94.46, -28.58) * mm});
            skLineSegment(sketch, "E23.top", {"start": v(-123.82, -53.98) * mm, "end": v(-94.46, -53.98) * mm});
            skLineSegment(sketch, "E23.left", {"start": v(-123.82, -28.58) * mm, "end": v(-123.82, -53.98) * mm});
            skLineSegment(sketch, "E23.right", {"start": v(-94.46, -28.58) * mm, "end": v(-94.46, -53.98) * mm});
            skLineSegment(sketch, "E24.bottom", {"start": v(-91.28, -53.98) * mm, "end": v(-32.54, -53.98) * mm});
            skLineSegment(sketch, "E24.top", {"start": v(-91.28, -28.58) * mm, "end": v(-32.54, -28.58) * mm});
            skLineSegment(sketch, "E24.left", {"start": v(-91.28, -53.98) * mm, "end": v(-91.28, -28.58) * mm});
            skLineSegment(sketch, "E24.right", {"start": v(-32.54, -53.98) * mm, "end": v(-32.54, -28.58) * mm});
            skLineSegment(sketch, "E25.bottom", {"start": v(-32.54, -25.4) * mm, "end": v(-91.28, -25.4) * mm});
            skLineSegment(sketch, "E25.top", {"start": v(-32.54, 25.4) * mm, "end": v(-91.28, 25.4) * mm});
            skLineSegment(sketch, "E25.left", {"start": v(-32.54, -25.4) * mm, "end": v(-32.54, 25.4) * mm});
            skLineSegment(sketch, "E25.right", {"start": v(-91.28, -25.4) * mm, "end": v(-91.28, 25.4) * mm});
            skLineSegment(sketch, "E26.bottom", {"start": v(-91.28, 28.57) * mm, "end": v(-32.54, 28.57) * mm});
            skLineSegment(sketch, "E26.top", {"start": v(-91.28, 53.98) * mm, "end": v(-32.54, 53.98) * mm});
            skLineSegment(sketch, "E26.left", {"start": v(-91.28, 28.57) * mm, "end": v(-91.28, 53.98) * mm});
            skLineSegment(sketch, "E26.right", {"start": v(-32.54, 28.57) * mm, "end": v(-32.54, 53.98) * mm});
            skLineSegment(sketch, "E27.bottom", {"start": v(-123.83, 53.98) * mm, "end": v(-94.46, 53.98) * mm});
            skLineSegment(sketch, "E27.top", {"start": v(-123.83, 28.57) * mm, "end": v(-94.46, 28.57) * mm});
            skLineSegment(sketch, "E27.left", {"start": v(-123.83, 53.98) * mm, "end": v(-123.83, 28.57) * mm});
            skLineSegment(sketch, "E27.right", {"start": v(-94.46, 53.98) * mm, "end": v(-94.46, 28.57) * mm});
            skLineSegment(sketch, "E28.bottom", {"start": v(-29.37, 53.98) * mm, "end": v(29.37, 53.98) * mm});
            skLineSegment(sketch, "E28.top", {"start": v(-29.37, 28.57) * mm, "end": v(29.37, 28.57) * mm});
            skLineSegment(sketch, "E28.left", {"start": v(-29.37, 53.98) * mm, "end": v(-29.37, 28.57) * mm});
            skLineSegment(sketch, "E28.right", {"start": v(29.37, 53.98) * mm, "end": v(29.37, 28.57) * mm});
            skLineSegment(sketch, "E29.bottom", {"start": v(32.54, 53.98) * mm, "end": v(91.28, 53.98) * mm});
            skLineSegment(sketch, "E29.top", {"start": v(32.54, 28.57) * mm, "end": v(91.28, 28.57) * mm});
            skLineSegment(sketch, "E29.left", {"start": v(32.54, 53.98) * mm, "end": v(32.54, 28.57) * mm});
            skLineSegment(sketch, "E29.right", {"start": v(91.28, 53.98) * mm, "end": v(91.28, 28.57) * mm});
            skLineSegment(sketch, "E30.bottom", {"start": v(94.46, 53.98) * mm, "end": v(123.82, 53.98) * mm});
            skLineSegment(sketch, "E30.top", {"start": v(94.46, 28.57) * mm, "end": v(123.82, 28.57) * mm});
            skLineSegment(sketch, "E30.left", {"start": v(94.46, 53.98) * mm, "end": v(94.46, 28.57) * mm});
            skLineSegment(sketch, "E30.right", {"start": v(123.82, 53.98) * mm, "end": v(123.82, 28.57) * mm});
            skLineSegment(sketch, "E31.bottom", {"start": v(94.46, 25.4) * mm, "end": v(123.82, 25.4) * mm});
            skLineSegment(sketch, "E31.top", {"start": v(94.46, -25.4) * mm, "end": v(123.82, -25.4) * mm});
            skLineSegment(sketch, "E31.left", {"start": v(94.46, 25.4) * mm, "end": v(94.46, -25.4) * mm});
            skLineSegment(sketch, "E31.right", {"start": v(123.82, 25.4) * mm, "end": v(123.82, -25.4) * mm});
            skLineSegment(sketch, "E32.bottom", {"start": v(94.46, -28.58) * mm, "end": v(123.82, -28.58) * mm});
            skLineSegment(sketch, "E32.top", {"start": v(94.46, -53.97) * mm, "end": v(123.82, -53.97) * mm});
            skLineSegment(sketch, "E32.left", {"start": v(94.46, -28.58) * mm, "end": v(94.46, -53.97) * mm});
            skLineSegment(sketch, "E32.right", {"start": v(123.82, -28.58) * mm, "end": v(123.82, -53.97) * mm});
            skLineSegment(sketch, "E33.bottom", {"start": v(32.54, -28.58) * mm, "end": v(91.28, -28.58) * mm});
            skLineSegment(sketch, "E33.top", {"start": v(32.54, -53.97) * mm, "end": v(91.28, -53.97) * mm});
            skLineSegment(sketch, "E33.left", {"start": v(32.54, -28.58) * mm, "end": v(32.54, -53.97) * mm});
            skLineSegment(sketch, "E33.right", {"start": v(91.28, -28.58) * mm, "end": v(91.28, -53.97) * mm});
            skLineSegment(sketch, "E34.bottom", {"start": v(91.28, -25.4) * mm, "end": v(32.54, -25.4) * mm});
            skLineSegment(sketch, "E34.top", {"start": v(91.28, 25.4) * mm, "end": v(32.54, 25.4) * mm});
            skLineSegment(sketch, "E34.left", {"start": v(91.28, -25.4) * mm, "end": v(91.28, 25.4) * mm});
            skLineSegment(sketch, "E34.right", {"start": v(32.54, -25.4) * mm, "end": v(32.54, 25.4) * mm});
            skLineSegment(sketch, "E35.bottom", {"start": v(29.37, 25.4) * mm, "end": v(-29.37, 25.4) * mm});
            skLineSegment(sketch, "E35.top", {"start": v(29.37, -25.4) * mm, "end": v(-29.37, -25.4) * mm});
            skLineSegment(sketch, "E35.left", {"start": v(29.37, 25.4) * mm, "end": v(29.37, -25.4) * mm});
            skLineSegment(sketch, "E35.right", {"start": v(-29.37, 25.4) * mm, "end": v(-29.37, -25.4) * mm});
            skLineSegment(sketch, "E36.bottom", {"start": v(-29.37, -28.58) * mm, "end": v(29.37, -28.58) * mm});
            skLineSegment(sketch, "E36.top", {"start": v(-29.37, -53.98) * mm, "end": v(29.37, -53.98) * mm});
            skLineSegment(sketch, "E36.left", {"start": v(-29.37, -28.58) * mm, "end": v(-29.37, -53.98) * mm});
            skLineSegment(sketch, "E36.right", {"start": v(29.37, -28.58) * mm, "end": v(29.37, -53.98) * mm});
            skLineSegment(sketch, "E37.bottom", {"start": v(-127, -57.15) * mm, "end": v(127, -57.15) * mm});
            skLineSegment(sketch, "E37.top", {"start": v(-127, 57.15) * mm, "end": v(127, 57.15) * mm});
            skLineSegment(sketch, "E37.left", {"start": v(-127, -57.15) * mm, "end": v(-127, 57.15) * mm});
            skLineSegment(sketch, "E37.right", {"start": v(127, -57.15) * mm, "end": v(127, 57.15) * mm});
            skSolve(sketch);
        }
        {
            var Q0;
            Q0=makeQuery(id+"F2.imprint","IMPRINT",FACE,{"disambiguationData":[TD([[makeQuery(id+"F2.imprint","IMPRINT",EDGE,{"derivedFrom":sQuery(id+"F2.wireOp",EDGE,"E22.bottom")}),-1.0]])]});
            extrude(context, id + "F3", {"entities" : qUnion([Q0]), "operationType" : NewBodyOperationType.ADD, "depth" : 6.35 * mm, "offsetDistance" : 25.4 * mm, "hasDraft" : true, "draftAngle" : 2 * degree});
        }
        {
            var Q0;
            Q0=makeQuery(id+"F1.opExtrude","CAP_FACE",FACE,{"disambiguationData":[OSD([sQuery(id+"F0.wireOp",EDGE,"E0.bottom"),sQuery(id+"F0.wireOp",EDGE,"E0.top"),sQuery(id+"F0.wireOp",EDGE,"E0.left"),sQuery(id+"F0.wireOp",EDGE,"E0.right"),sQuery(id+"F0.wireOp",EDGE,"E1.0"),sQuery(id+"F0.wireOp",EDGE,"E1.1"),sQuery(id+"F0.wireOp",EDGE,"E1.2"),sQuery(id+"F0.wireOp",EDGE,"E1.3"),sQuery(id+"F0.wireOp",EDGE,"E12.bottom"),sQuery(id+"F0.wireOp",EDGE,"E12.top"),sQuery(id+"F0.wireOp",EDGE,"E14.bottom"),sQuery(id+"F0.wireOp",EDGE,"E14.top"),sQuery(id+"F0.wireOp",EDGE,"E15.left"),sQuery(id+"F0.wireOp",EDGE,"E15.right"),sQuery(id+"F0.wireOp",EDGE,"E17.left"),sQuery(id+"F0.wireOp",EDGE,"E17.right"),sQuery(id+"F0.wireOp",EDGE,"E19.left"),sQuery(id+"F0.wireOp",EDGE,"E19.right"),sQuery(id+"F0.wireOp",EDGE,"E21.left"),sQuery(id+"F0.wireOp",EDGE,"E21.right")])],"isStart":false});
            var Q1;
            Q1=makeQuery(id+"F3.opExtrude","CAP_FACE",FACE,{"disambiguationData":[OSD([sQuery(id+"F2.wireOp",EDGE,"E22.bottom"),sQuery(id+"F2.wireOp",EDGE,"E22.top"),sQuery(id+"F2.wireOp",EDGE,"E22.left"),sQuery(id+"F2.wireOp",EDGE,"E22.right"),sQuery(id+"F2.wireOp",EDGE,"E23.bottom"),sQuery(id+"F2.wireOp",EDGE,"E23.top"),sQuery(id+"F2.wireOp",EDGE,"E23.left"),sQuery(id+"F2.wireOp",EDGE,"E23.right"),sQuery(id+"F2.wireOp",EDGE,"E24.bottom"),sQuery(id+"F2.wireOp",EDGE,"E24.top"),sQuery(id+"F2.wireOp",EDGE,"E24.left"),sQuery(id+"F2.wireOp",EDGE,"E24.right"),sQuery(id+"F2.wireOp",EDGE,"E25.bottom"),sQuery(id+"F2.wireOp",EDGE,"E25.top"),sQuery(id+"F2.wireOp",EDGE,"E25.left"),sQuery(id+"F2.wireOp",EDGE,"E25.right"),sQuery(id+"F2.wireOp",EDGE,"E26.bottom"),sQuery(id+"F2.wireOp",EDGE,"E26.top"),sQuery(id+"F2.wireOp",EDGE,"E26.left"),sQuery(id+"F2.wireOp",EDGE,"E26.right"),sQuery(id+"F2.wireOp",EDGE,"E27.bottom"),sQuery(id+"F2.wireOp",EDGE,"E27.top"),sQuery(id+"F2.wireOp",EDGE,"E27.left"),sQuery(id+"F2.wireOp",EDGE,"E27.right"),sQuery(id+"F2.wireOp",EDGE,"E28.bottom"),sQuery(id+"F2.wireOp",EDGE,"E28.top"),sQuery(id+"F2.wireOp",EDGE,"E28.left"),sQuery(id+"F2.wireOp",EDGE,"E28.right"),sQuery(id+"F2.wireOp",EDGE,"E29.bottom"),sQuery(id+"F2.wireOp",EDGE,"E29.top"),sQuery(id+"F2.wireOp",EDGE,"E29.left"),sQuery(id+"F2.wireOp",EDGE,"E29.right"),sQuery(id+"F2.wireOp",EDGE,"E30.bottom"),sQuery(id+"F2.wireOp",EDGE,"E30.top"),sQuery(id+"F2.wireOp",EDGE,"E30.left"),sQuery(id+"F2.wireOp",EDGE,"E30.right"),sQuery(id+"F2.wireOp",EDGE,"E31.bottom"),sQuery(id+"F2.wireOp",EDGE,"E31.top"),sQuery(id+"F2.wireOp",EDGE,"E31.left"),sQuery(id+"F2.wireOp",EDGE,"E31.right"),sQuery(id+"F2.wireOp",EDGE,"E32.bottom"),sQuery(id+"F2.wireOp",EDGE,"E32.top"),sQuery(id+"F2.wireOp",EDGE,"E32.left"),sQuery(id+"F2.wireOp",EDGE,"E32.right"),sQuery(id+"F2.wireOp",EDGE,"E33.bottom"),sQuery(id+"F2.wireOp",EDGE,"E33.top"),sQuery(id+"F2.wireOp",EDGE,"E33.left"),sQuery(id+"F2.wireOp",EDGE,"E33.right"),sQuery(id+"F2.wireOp",EDGE,"E34.bottom"),sQuery(id+"F2.wireOp",EDGE,"E34.top"),sQuery(id+"F2.wireOp",EDGE,"E34.left"),sQuery(id+"F2.wireOp",EDGE,"E34.right"),sQuery(id+"F2.wireOp",EDGE,"E35.bottom"),sQuery(id+"F2.wireOp",EDGE,"E35.top"),sQuery(id+"F2.wireOp",EDGE,"E35.left"),sQuery(id+"F2.wireOp",EDGE,"E35.right"),sQuery(id+"F2.wireOp",EDGE,"E36.bottom"),sQuery(id+"F2.wireOp",EDGE,"E36.top"),sQuery(id+"F2.wireOp",EDGE,"E36.left"),sQuery(id+"F2.wireOp",EDGE,"E36.right"),sQuery(id+"F2.wireOp",EDGE,"E37.bottom"),sQuery(id+"F2.wireOp",EDGE,"E37.top"),sQuery(id+"F2.wireOp",EDGE,"E37.left"),sQuery(id+"F2.wireOp",EDGE,"E37.right")])],"isStart":false});
            fillet(context, id + "F4", {"entities" : qUnion([Q0, Q1]), "radius" : 0.28 * mm, "tangentPropagation" : true, "allowEdgeOverflow" : false});
        }
    });
